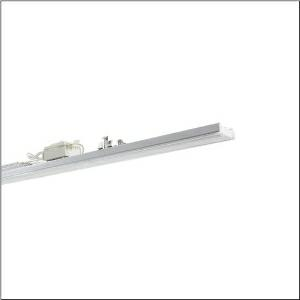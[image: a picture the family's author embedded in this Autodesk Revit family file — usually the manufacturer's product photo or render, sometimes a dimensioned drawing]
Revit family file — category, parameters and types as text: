
# Revit family: licross_r__11_recessed_mo_51tl1e7n485g_323e
name_source: partatom
category: Lighting Fixtures
units: mm (PartAtom-declared; Revit-internal decimal feet)

## family parameters
Cut with Voids When Loaded = No
Host = Face
Light Source = No
Part Type = Normal
Room Calculation Point = No
Round Connector Dimension = Use Diameter
Shared = No

## types (1)
- Licross® 11 Recessed MO (1 x LED, 8660 lm, 48.5 W, 4000K)
    Apparent Load = 49 VA
    CIE Flux Codes = 85 95 99 100 100
    Color Rendering = 80
    Color Temperature = 4000K
    Default Elevation = 1800 mm
    Description = Licross® 11 Recessed MO, luminaire insert, of sheet steel, coil coated, white, length: 1.500mm, width: 66mm, height: 67mm, LED rated luminous flux: 8.660lm, light colour: 840, control gear: ON/OFF, with plug, 3-pole, with phase selection, mains connection: 220..240V, AC, 50/60Hz, rated input power: 49W, halogen-free wiring, primary light control with lens, of plastic, primary optical cover: cover, of PMMA, light emission: direct distribution, primary light characteristic: symmetric, protection rating (complete): IP40, insulation class (complete): insulation class I (protective earthing), certification: CE, ENEC, VDE, UKCA, protection symbol: D if used in an environment without relevant dust loads with corresponding accessories, impact resistance: IK06, permissible ambient temperature for indoor applications: -35..+35°C, corresponds to IFS (International Featured Standards) requirements for safety and quality in the food industry, reducing of maximum allowable ambient temperature of 5°C with ceiling mounting, packaging unit: 1 piece
    Height = 58 mm
    Lamp = 1 x LED
    Lamp Light Flux = 8660 lm
    Lamp Power = 48.5 W
    Lamp count = 1
    Length = 1500 mm
    Luminous efficacy = 179 lm/W
    Manufacturer = Siteco
    ModVariant = No
    Model = 51TL1E7N485G
    Mounting Place = Ceiling
    Mounting Type = Pendant
    Number of Poles = 1
    OnlyDefault = Yes
    Power Factor = 1
    Product Name = Licross® 11 Recessed MO
    Product group = luminaire insert
    ProductGroupID = 902
    Protection Class = Protection class I
    Protection Degree = IP 40
    RLX_Detail_Level = 1
    RLX_Emergency_Light_Flux = 0 lm
    RLX_Emergency_Type = 0
    RLX_Emergency_Type_DB = No
    RlxData = <blob elided: 20865 chars, md5=ac82b39c>
    Socket = socket
    Standby Power = 0 W
    System Light Flux = 8660 lm
    System Power = 49 W
    Type Comments = Product without accessories
    Type Image = l_1296930.jpg
    URL = http://relux.com
    VarID = ---
    Voltage = 0 V
    Weight = 0.00 kg
    Width = 66 mm

## geometry (parser evidence)
native form markers: Blend x4, Sweep x9
no freeform markers — native parametric forms only
